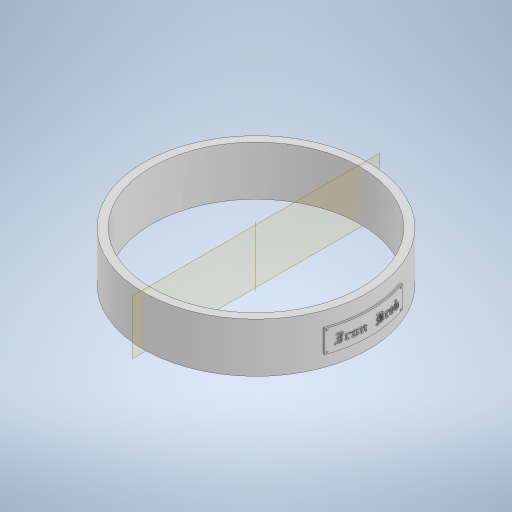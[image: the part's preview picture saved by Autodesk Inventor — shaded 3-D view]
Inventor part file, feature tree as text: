
AUTODESK INVENTOR PART (.ipt)
format: ipt  version: 2023 (Build 270158000, 158)  size: 3,399,168 bytes
history: native  units: in
note: dims shown in document units (in); Inventor stores cm internally (conversion verified against a paired STEP export)
features: emboss x3, pattern_circular x3, other x2, extrude x1, plane x1, fillet x1, sketch x1
ambient origin geometry x8: Origin, YZ Plane, XZ Plane, XY Plane, X Axis, Y Axis, Z Axis, Center Point
bodies: Solid1 (feature_tree)
feature tree (12):
  extrude  "Extrusion1"  Depth=0.3937in
  plane  "Work Plane1"
  other  "Text"
  emboss  "Emboss4"
  emboss  "Emboss5"
  emboss  "Emboss6"
  fillet  "Rivots"  Radius=0.8661in
  pattern_circular  "Circular Pattern1"  Count=6  [1 undecoded]
  pattern_circular  "Circular Pattern2"  [2 undecoded]
  pattern_circular  "Circular Pattern3"  [2 undecoded]
  sketch  "Sketch1"  dims[d0=3.937in d1=3.6614in d2=0.8661in d3=0.0in d4=2.3622in d6=0.4546in d10=0.0in d11=0.3937in d12=1.378in d19=0.0in d20=0.0in d21=0.0295in d22=0.0in d23=0.0197in d24=0.0in d25=0.0295in d26=0.0295in d27=0.0295in d28=0.0157in d29=0.0in d30=0.0138in d31=0.7874in d32=360.0deg d34=0.7874in d35=360.0deg d37=0.7874in d38=360.0deg d33=0.0in]
  other  "NamePlate"
note: 5 required parameter values undecoded (feature->parameter linkage not recoverable at this tier; creation-order binding heuristic only, values carry confidence <= 0.55)
